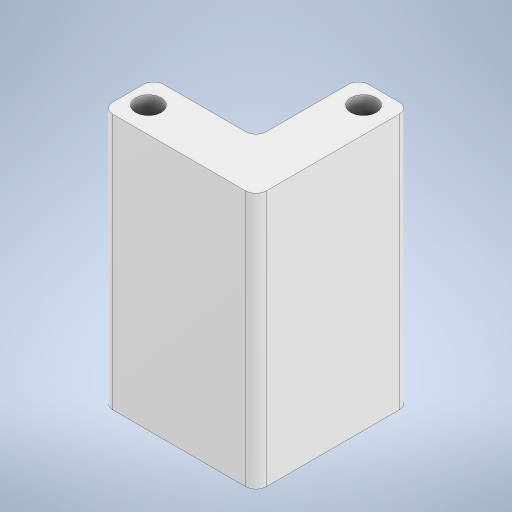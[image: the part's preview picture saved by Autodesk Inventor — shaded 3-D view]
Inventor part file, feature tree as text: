
AUTODESK INVENTOR PART (.ipt)
format: ipt  version: 2024 (Build 280153000, 153)  size: 231,424 bytes
history: native  units: in
note: dims shown in document units (in); Inventor stores cm internally (conversion verified against a paired STEP export)
features: fillet x2, sketch x2, extrude x1, hole x1
ambient origin geometry x8: Origin, YZ Plane, XZ Plane, XY Plane, X Axis, Y Axis, Z Axis, Center Point
bodies: Body1 (feature_tree)
feature tree (6):
  extrude  "Extrusion2"  Depth=1.1811in
  hole  "Hole1"  [1 undecoded]
  fillet  "Fillet1"  Radius=1.9685in
  fillet  "Fillet2"  Radius=0.1575in
  sketch  "Sketch2"  dims[d4=1.1811in d5=1.1811in]
  sketch  "Sketch3"  dims[d6=0.7874in d7=0.7874in d8=1.9685in d9=0.0in d10=0.1969in d11=0.2953in d12=0.1476in d13=0.0984in d14=90.0deg d15=0.3937in d16=0.8108in d17=0.1575in d18=0.1969in d19=0.1575in d20=0.1969in d21=0.0787in d22=0.0787in]
note: 1 required parameter value undecoded (feature->parameter linkage not recoverable at this tier; creation-order binding heuristic only, values carry confidence <= 0.55)
